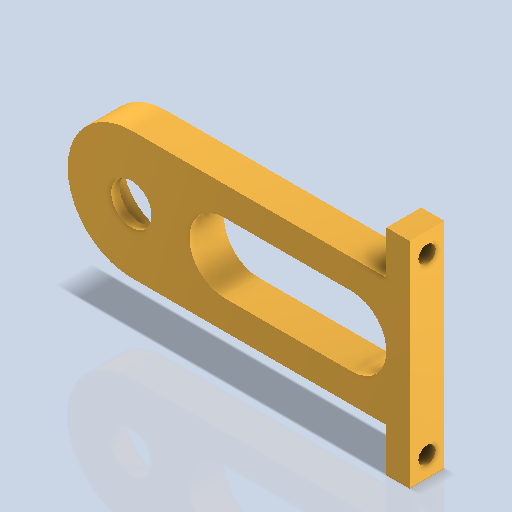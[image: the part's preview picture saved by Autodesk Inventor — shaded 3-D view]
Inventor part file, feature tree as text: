
AUTODESK INVENTOR PART (.ipt)
format: ipt  version: 2024.2 (Build 282272000, 272)  size: 272,896 bytes
history: native  units: mm
features: sketch x5, hole x3, extrude x2
ambient origin geometry x8: Origin, YZ Plane, XZ Plane, XY Plane, X Axis, Y Axis, Z Axis, Center Point
bodies: Volumenkörper1 (feature_tree)
feature tree (10):
  extrude  "Extrusion1"  Depth=16.0mm
  hole  "Bohrung1"  [1 undecoded]
  hole  "Bohrung2"  [1 undecoded]
  extrude  "Extrusion2"  Depth=48.0mm
  hole  "Bohrung3"  [1 undecoded]
  sketch  "Skizze1"  dims[d0=192.0mm d1=16.0mm]
  sketch  "Skizze2"  dims[d2=30.0mm d3=44.0mm]
  sketch  "Skizze3"  dims[d4=24.0mm d5=0.0mm]
  sketch  "Skizze4"  dims[d6=60.0mm d7=8.0mm d8=6.0mm d9=2.5mm d10=90.0deg d11=18.0mm d12=0.0mm]
  sketch  "Skizze5"  dims[d13=28.0mm d14=6.0mm d15=4.0mm d16=2.0mm d17=90.0deg d18=18.0mm d19=0.0mm d20=88.0mm d21=48.0mm d22=24.0mm d23=24.0mm d24=0.0mm d25=12.0mm d26=6.0mm d27=4.0mm d28=2.0mm d29=90.0deg d30=8.0mm d31=0.0mm d32=120.0mm d33=60.0mm]
note: 3 required parameter values undecoded (feature->parameter linkage not recoverable at this tier; creation-order binding heuristic only, values carry confidence <= 0.55)
